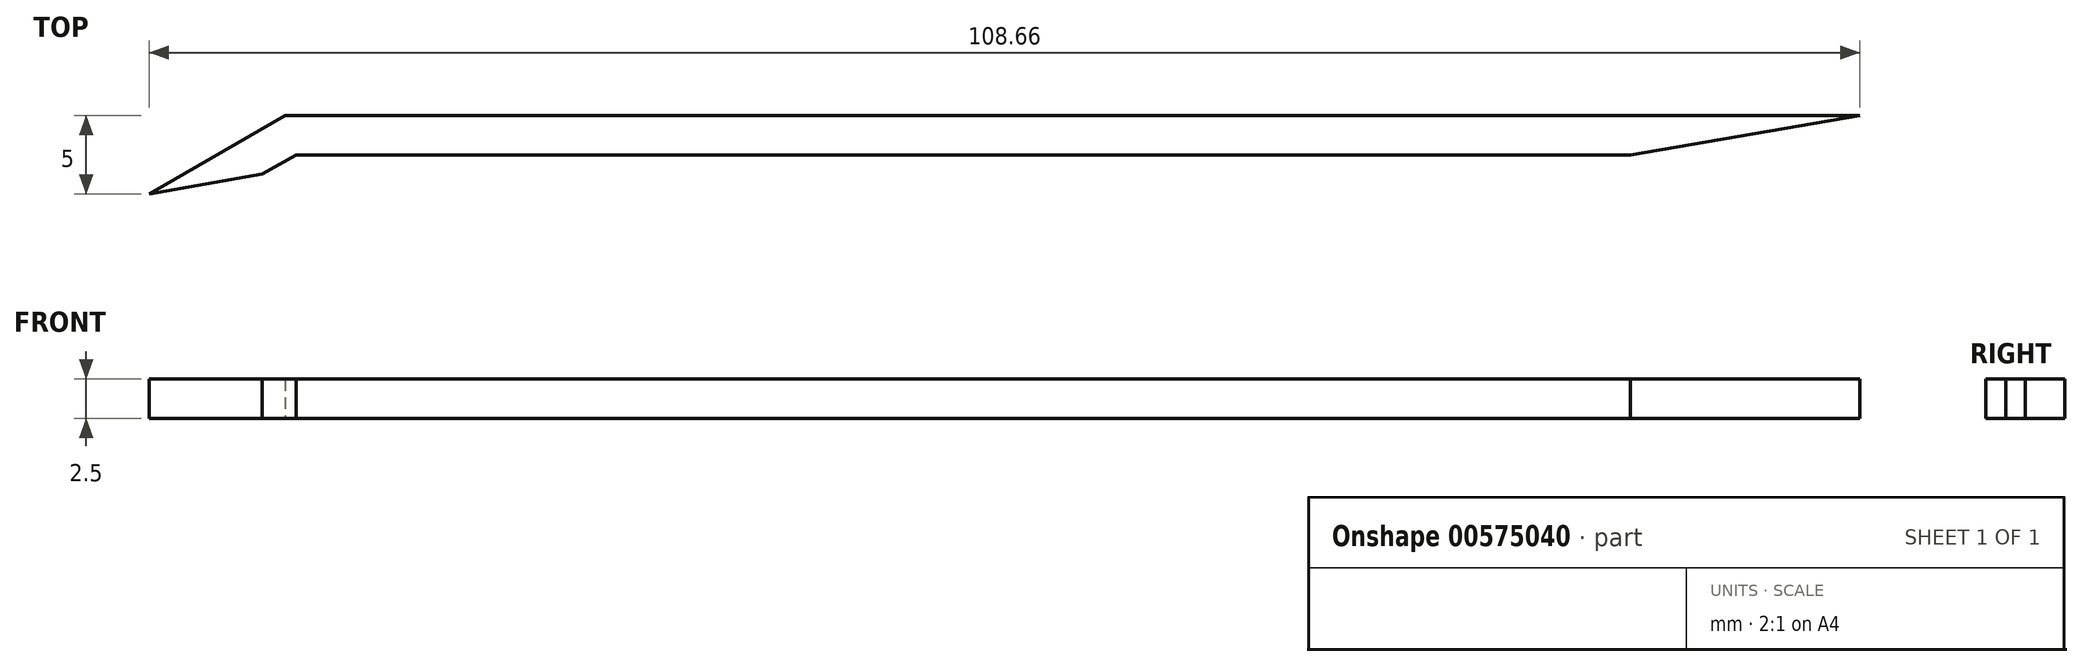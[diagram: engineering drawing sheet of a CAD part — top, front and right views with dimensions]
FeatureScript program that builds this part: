
annotation { "Feature Type Name" : "Feature", "Feature Type Description" : "" }
export const myFeature = defineFeature(function(context is Context, id is Id, definition is map)
    precondition{}
    {
        {
            var Q0;
            Q0=qCreatedBy(makeId("Top.planeOp"),FACE);
            var sketch = newSketch(context, id + "F0", { "sketchPlane" : qUnion([Q0])});
            skLineSegment(sketch, "E0", {"start": v(52.6, 2.5) * mm, "end": v(-47.4, 2.5) * mm});
            skLineSegment(sketch, "E1", {"start": v(38.04, 0) * mm, "end": v(-46.72, 0) * mm});
            skLineSegment(sketch, "E2", {"start": v(52.6, 2.5) * mm, "end": v(38.04, 0) * mm});
            skLineSegment(sketch, "E3", {"start": v(-47.4, 2.5) * mm, "end": v(-56.05, -2.5) * mm});
            skLineSegment(sketch, "E4", {"start": v(-56.05, -2.5) * mm, "end": v(-48.86, -1.23) * mm});
            skLineSegment(sketch, "E5", {"start": v(-48.86, -1.23) * mm, "end": v(-46.72, 0) * mm});
            skSolve(sketch);
        }
        {
            var Q0;
            Q0 = qSketchRegion(id + "F0", true);
            extrude(context, id + "F1", {"entities" : qUnion([Q0]), "depth" : 2.5 * mm, "offsetDistance" : 25 * mm});
        }
    });
